# Revit family: BSC-Class-II_Type-B1_NuAire_Labgard_427
name_source: partatom
category: Mechanical Equipment
units: mm (PartAtom-declared; Revit-internal decimal feet)

## family parameters
Always vertical = Yes
Classification Number = 23.40.70.11.11.11.11
Cut with Voids When Loaded = No
Maintain Annotation Orientation = No
Part Type = Normal
Room Calculation Point = No
Round Connector Dimension = Use Radius
Shared = No
Work Plane-Based = No

## types (4) — shared parameters
Assembly Code = E1020720
Construction Details = http://www.arcat.com
DEPTH = 2' - 4"
Default Elevation = 0' - 0"
Description = Class II Type B1 Biological Safety Cabinet
EXHAUST RING BACK = 1' - 0"
EXHAUST RING SIDE = 1' - 4 1/8"
Exhaust Flow = 271 CFM
INTAKE RING BACK = 1' - 0"
INTAKE RING SIDE = 1' - 2 5/16"
Keynote = 11 53 00
Manufacturer = Nuaire Inc
Manufacturer Fax = 763-553-0459
Manufacturer Website = http://www.nuaire.com
Product Data = http://www.arcat.com
Product Properties = http://www.nuaire.com
RING SIZE = 0' - 6"
Revision = R1_12/2015
Room Inflow = 105 CFM
Sales Information = http://www.nuaire.com
Specification = http://www.arcat.com
Type Comments = Contact Sales for Info: 800-328-3352, 888-4-NUAIRE, www.nuaire.com
URL = http://www.nuaire.com
WIDTH = 4' - 5 5/8"
WORK SURFACE HEIGHT = 2' - 2 1/2"
control panel = 1' - 6 13/16"

## per-type parameters (varying)
| type | Model |
| 600 - 36 WORK SURFACE HEIGHT | NU-427-600 |
| 400 - 36 WORK SURFACE HEIGHT | NU-427-400 |
| 600 - 30 WORK SURFACE HEIGHT | NU-427-600 |
| 400 - 30 WORK SURFACE HEIGHT | NU-427-400 |

## geometry (parser evidence)
native form markers: Blend x12, Sweep x3
no freeform markers — native parametric forms only
